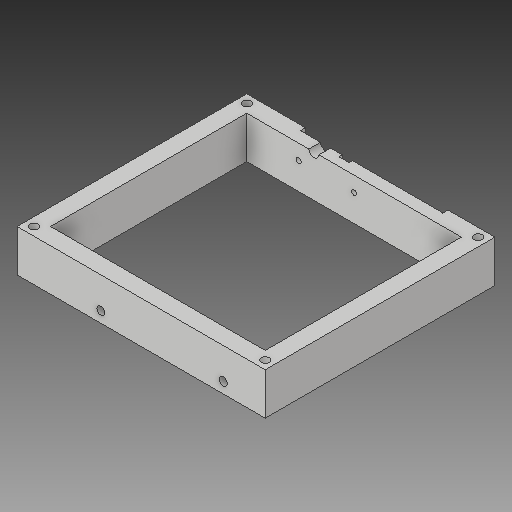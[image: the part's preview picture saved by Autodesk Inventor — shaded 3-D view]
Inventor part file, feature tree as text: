
AUTODESK INVENTOR PART (.ipt)
format: ipt  version: 2017 (Build 210142000, 142)  size: 230,400 bytes
history: native  units: mm
features: extrude x12, sketch x12, other x2, revolve x1, pattern_linear x1, mirror x1
ambient origin geometry x8: Origin, YZ Plane, XZ Plane, XY Plane, X Axis, Y Axis, Z Axis, Center Point
bodies: Body1 (feature_tree)
feature tree (29):
  other  "Твердое тело1"
  extrude  "Выдавливание1"  Depth=148.0mm
  extrude  "Выдавливание2"  Depth=10.0mm
  revolve  "Вращение3"
  extrude  "Выдавливание4"  Depth=10.0mm
  extrude  "Выдавливание5"  Depth=10.0mm
  extrude  "Выдавливание6"  Depth=10.0mm
  extrude  "Выдавливание7"  Depth=25.0mm TaperAngle=0.0deg
  pattern_linear  "Прямоуг.массив3"  Spacing1=117.0mm  [1 undecoded]
  other  "РабПлоскость1"
  mirror  "Зеркальное отражение1"
  extrude  "Выдавливание8"  Depth=5.0mm
  extrude  "Выдавливание9"  Depth=5.0mm
  extrude  "Выдавливание10"  Depth=10.0mm TaperAngle=0.0deg
  extrude  "Выдавливание11"  Depth=5.0mm
  extrude  "Выдавливание12"  Depth=50.0mm
  extrude  "Выдавливание13"  Depth=6.0mm
  sketch  "Эскиз1"
  sketch  "Эскиз2"
  sketch  "Эскиз6"
  sketch  "Эскиз8"
  sketch  "Эскиз9"
  sketch  "Эскиз10"
  sketch  "Эскиз14"
  sketch  "Эскиз15"
  sketch  "Эскиз16"
  sketch  "Эскиз17"
  sketch  "Эскиз18"
  sketch  "Эскиз19"
note: 1 required parameter value undecoded (feature->parameter linkage not recoverable at this tier; creation-order binding heuristic only, values carry confidence <= 0.55)
